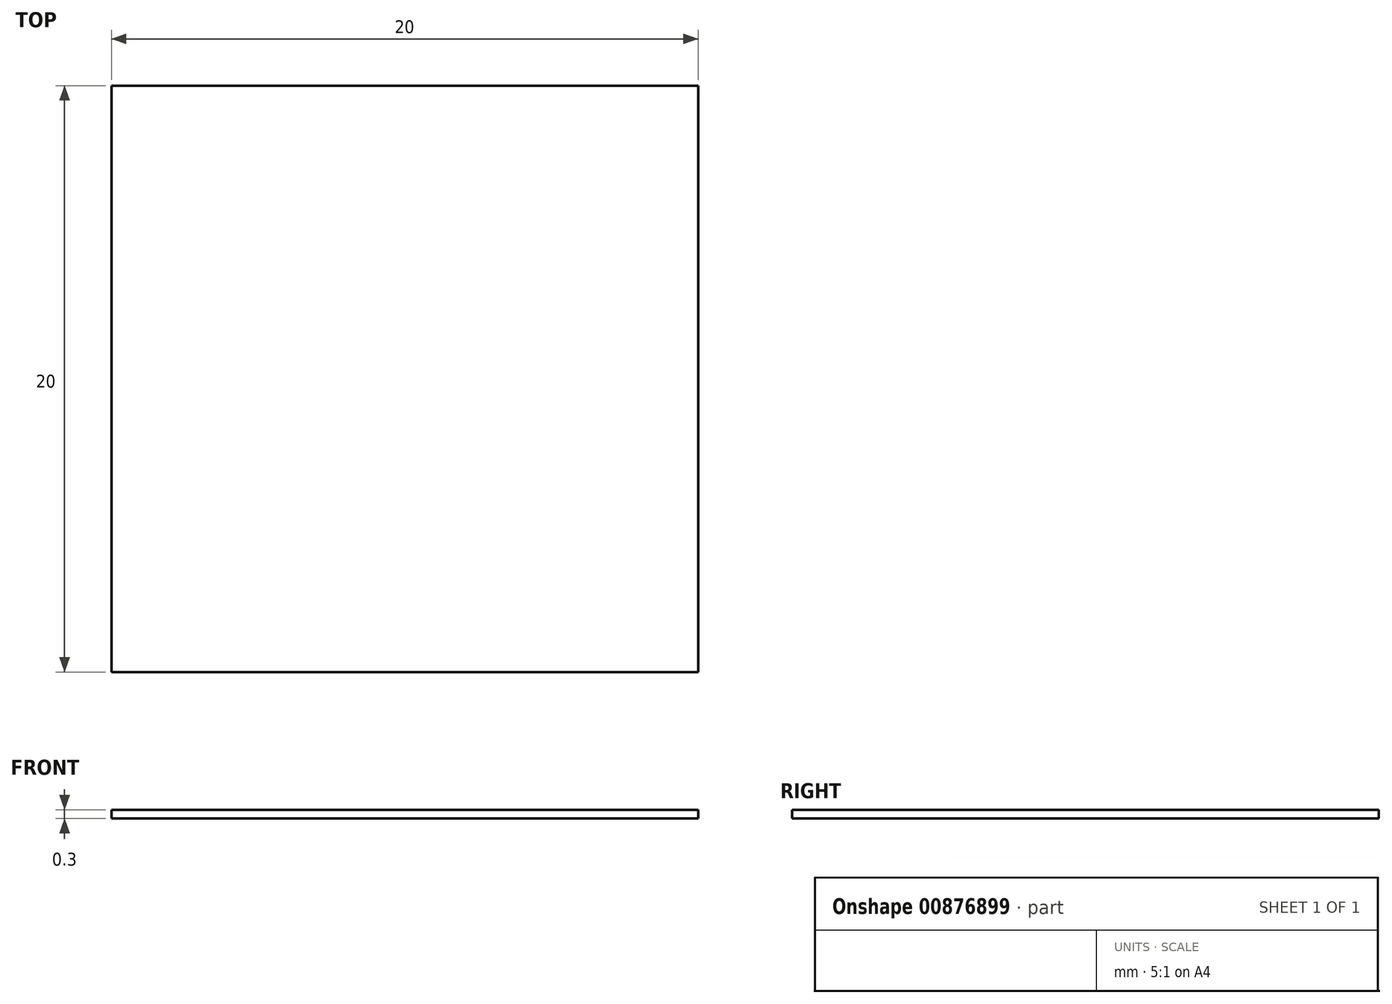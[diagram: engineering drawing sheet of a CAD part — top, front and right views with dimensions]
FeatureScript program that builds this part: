
annotation { "Feature Type Name" : "Feature", "Feature Type Description" : "" }
export const myFeature = defineFeature(function(context is Context, id is Id, definition is map)
    precondition{}
    {
        {
            var Q0;
            Q0=qCreatedBy(makeId("Top.planeOp"),FACE);
            var sketch = newSketch(context, id + "F0", { "sketchPlane" : qUnion([Q0])});
            skLineSegment(sketch, "E0.bottom", {"start": v(-10, 10) * mm, "end": v(10, 10) * mm});
            skLineSegment(sketch, "E0.top", {"start": v(-10, -10) * mm, "end": v(10, -10) * mm});
            skLineSegment(sketch, "E0.left", {"start": v(-10, 10) * mm, "end": v(-10, -10) * mm});
            skLineSegment(sketch, "E0.right", {"start": v(10, 10) * mm, "end": v(10, -10) * mm});
            skSolve(sketch);
        }
        {
            var Q0;
            Q0=makeQuery(id+"F0.imprint","IMPRINT",FACE,{"disambiguationData":[TD([[makeQuery(id+"F0.imprint","IMPRINT",EDGE,{"derivedFrom":sQuery(id+"F0.wireOp",EDGE,"E0.bottom")}),-1.0]])]});
            extrude(context, id + "F1", {"entities" : qUnion([Q0]), "depth" : 0.3 * mm, "offsetDistance" : 25 * mm});
        }
    });
